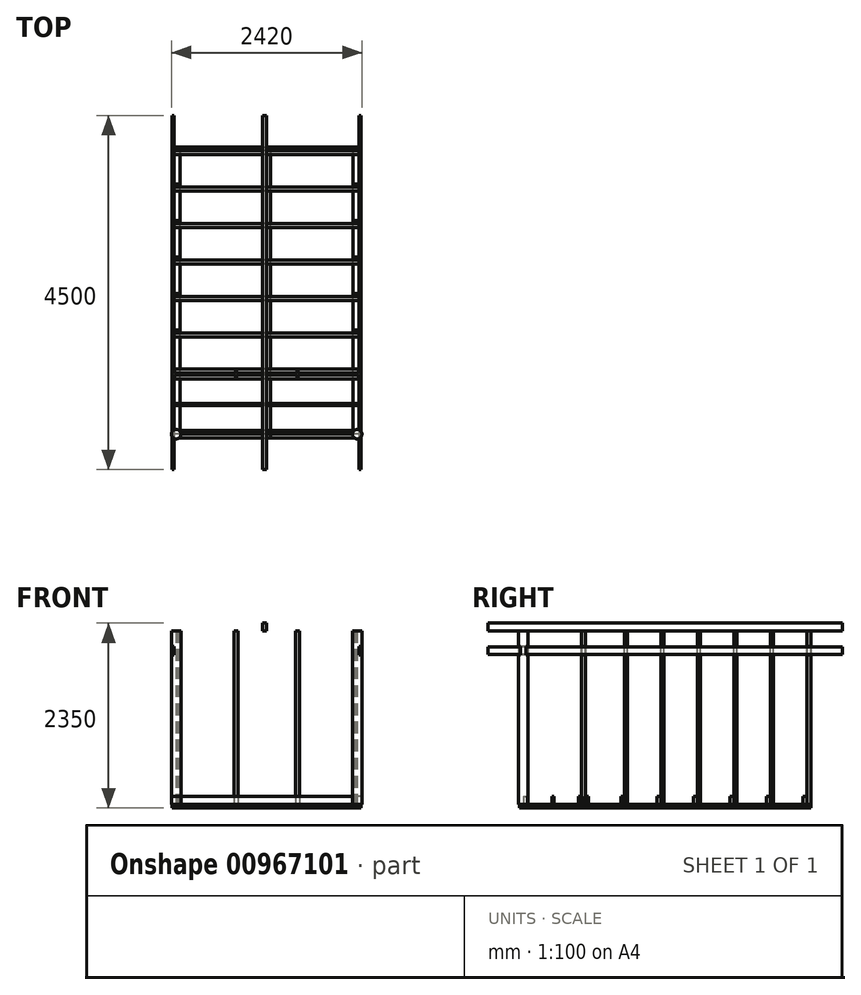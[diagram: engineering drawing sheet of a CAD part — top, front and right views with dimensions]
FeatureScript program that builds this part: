
annotation { "Feature Type Name" : "Feature", "Feature Type Description" : "" }
export const myFeature = defineFeature(function(context is Context, id is Id, definition is map)
    precondition{}
    {
        {
            var Q0;
            Q0=qCreatedBy(makeId("Top.planeOp"),FACE);
            var sketch = newSketch(context, id + "F0", { "sketchPlane" : qUnion([Q0])});
            skLineSegment(sketch, "E0.bottom", {"start": v(-1200, 0) * mm, "end": v(-1100, 0) * mm});
            skLineSegment(sketch, "E0.top", {"start": v(-1200, 3700) * mm, "end": v(-1100, 3700) * mm});
            skLineSegment(sketch, "E0.left", {"start": v(-1200, 0) * mm, "end": v(-1200, 3700) * mm});
            skLineSegment(sketch, "E0.right", {"start": v(-1100, 0) * mm, "end": v(-1100, 3700) * mm});
            skLineSegment(sketch, "E1.bottom", {"start": v(-1099, 0) * mm, "end": v(-51, 0) * mm});
            skLineSegment(sketch, "E1.top", {"start": v(-1099, 100) * mm, "end": v(-51, 100) * mm});
            skLineSegment(sketch, "E1.left", {"start": v(-1099, 0) * mm, "end": v(-1099, 100) * mm});
            skLineSegment(sketch, "E1.right", {"start": v(-51, 0) * mm, "end": v(-51, 100) * mm});
            skLineSegment(sketch, "E2.bottom", {"start": v(-50, 0) * mm, "end": v(50, 0) * mm});
            skLineSegment(sketch, "E2.top", {"start": v(-50, 3700) * mm, "end": v(50, 3700) * mm});
            skLineSegment(sketch, "E2.left", {"start": v(-50, 0) * mm, "end": v(-50, 3700) * mm});
            skLineSegment(sketch, "E2.right", {"start": v(50, 0) * mm, "end": v(50, 3700) * mm});
            skLineSegment(sketch, "E3.bottom", {"start": v(51, 0) * mm, "end": v(1099, 0) * mm});
            skLineSegment(sketch, "E3.top", {"start": v(51, 100) * mm, "end": v(1099, 100) * mm});
            skLineSegment(sketch, "E3.left", {"start": v(51, 0) * mm, "end": v(51, 100) * mm});
            skLineSegment(sketch, "E3.right", {"start": v(1099, 0) * mm, "end": v(1099, 100) * mm});
            skLineSegment(sketch, "E4.bottom", {"start": v(1100, 0) * mm, "end": v(1200, 0) * mm});
            skLineSegment(sketch, "E4.top", {"start": v(1100, 3700) * mm, "end": v(1200, 3700) * mm});
            skLineSegment(sketch, "E4.left", {"start": v(1100, 0) * mm, "end": v(1100, 3700) * mm});
            skLineSegment(sketch, "E4.right", {"start": v(1200, 0) * mm, "end": v(1200, 3700) * mm});
            skLineSegment(sketch, "E5.bottom", {"start": v(51, 3700) * mm, "end": v(1099, 3700) * mm});
            skLineSegment(sketch, "E5.top", {"start": v(51, 3600) * mm, "end": v(1099, 3600) * mm});
            skLineSegment(sketch, "E5.left", {"start": v(51, 3700) * mm, "end": v(51, 3600) * mm});
            skLineSegment(sketch, "E5.right", {"start": v(1099, 3700) * mm, "end": v(1099, 3600) * mm});
            skLineSegment(sketch, "E6.bottom", {"start": v(-1099, 3700) * mm, "end": v(-51, 3700) * mm});
            skLineSegment(sketch, "E6.top", {"start": v(-1099, 3600) * mm, "end": v(-51, 3600) * mm});
            skLineSegment(sketch, "E6.left", {"start": v(-1099, 3700) * mm, "end": v(-1099, 3600) * mm});
            skLineSegment(sketch, "E6.right", {"start": v(-51, 3700) * mm, "end": v(-51, 3600) * mm});
            skLineSegment(sketch, "E7", {"start": v(0, 0) * mm, "end": v(0, 3700) * mm, "construction": true});
            skSolve(sketch);
        }
        {
            var Q0;
            Q0 = qSketchRegion(id + "F0", true);
            extrude(context, id + "F1", {"entities" : qUnion([Q0]), "depth" : 50 * mm, "offsetDistance" : 25 * mm});
        }
        {
            var Q0;
            Q0=qCreatedBy(makeId("Right.planeOp"),FACE);
            var sketch = newSketch(context, id + "F2", { "sketchPlane" : qUnion([Q0])});
            skLineSegment(sketch, "E8.bottom", {"start": v(50, 150) * mm, "end": v(100, 150) * mm});
            skLineSegment(sketch, "E8.top", {"start": v(50, 50) * mm, "end": v(100, 50) * mm});
            skLineSegment(sketch, "E8.left", {"start": v(50, 150) * mm, "end": v(50, 50) * mm});
            skLineSegment(sketch, "E8.right", {"start": v(100, 150) * mm, "end": v(100, 50) * mm});
            skLineSegment(sketch, "E9.bottom", {"start": v(412.5, 150) * mm, "end": v(437.5, 150) * mm});
            skLineSegment(sketch, "E9.top", {"start": v(412.5, 50) * mm, "end": v(437.5, 50) * mm});
            skLineSegment(sketch, "E9.left", {"start": v(412.5, 150) * mm, "end": v(412.5, 50) * mm});
            skLineSegment(sketch, "E9.right", {"start": v(437.5, 150) * mm, "end": v(437.5, 50) * mm});
            skLineSegment(sketch, "E10.bottom", {"start": v(750, 150) * mm, "end": v(800, 150) * mm});
            skLineSegment(sketch, "E10.top", {"start": v(750, 50) * mm, "end": v(800, 50) * mm});
            skLineSegment(sketch, "E10.left", {"start": v(750, 150) * mm, "end": v(750, 50) * mm});
            skLineSegment(sketch, "E10.right", {"start": v(800, 150) * mm, "end": v(800, 50) * mm});
            skLineSegment(sketch, "E11.bottom", {"start": v(825, 150) * mm, "end": v(875, 150) * mm});
            skLineSegment(sketch, "E11.top", {"start": v(825, 50) * mm, "end": v(875, 50) * mm});
            skLineSegment(sketch, "E11.left", {"start": v(825, 150) * mm, "end": v(825, 50) * mm});
            skLineSegment(sketch, "E11.right", {"start": v(875, 150) * mm, "end": v(875, 50) * mm});
            skLineSegment(sketch, "E12.bottom", {"start": v(1287.5, 150) * mm, "end": v(1337.5, 150) * mm});
            skLineSegment(sketch, "E12.top", {"start": v(1287.5, 50) * mm, "end": v(1337.5, 50) * mm});
            skLineSegment(sketch, "E12.left", {"start": v(1287.5, 150) * mm, "end": v(1287.5, 50) * mm});
            skLineSegment(sketch, "E12.right", {"start": v(1337.5, 150) * mm, "end": v(1337.5, 50) * mm});
            skLineSegment(sketch, "E13.bottom", {"start": v(1750, 150) * mm, "end": v(1800, 150) * mm});
            skLineSegment(sketch, "E13.top", {"start": v(1750, 50) * mm, "end": v(1800, 50) * mm});
            skLineSegment(sketch, "E13.left", {"start": v(1750, 150) * mm, "end": v(1750, 50) * mm});
            skLineSegment(sketch, "E13.right", {"start": v(1800, 150) * mm, "end": v(1800, 50) * mm});
            skLineSegment(sketch, "E14.bottom", {"start": v(2212.5, 150) * mm, "end": v(2262.5, 150) * mm});
            skLineSegment(sketch, "E14.top", {"start": v(2212.5, 50) * mm, "end": v(2262.5, 50) * mm});
            skLineSegment(sketch, "E14.left", {"start": v(2212.5, 150) * mm, "end": v(2212.5, 50) * mm});
            skLineSegment(sketch, "E14.right", {"start": v(2262.5, 150) * mm, "end": v(2262.5, 50) * mm});
            skLineSegment(sketch, "E15.bottom", {"start": v(2675, 150) * mm, "end": v(2725, 150) * mm});
            skLineSegment(sketch, "E15.top", {"start": v(2675, 50) * mm, "end": v(2725, 50) * mm});
            skLineSegment(sketch, "E15.left", {"start": v(2675, 150) * mm, "end": v(2675, 50) * mm});
            skLineSegment(sketch, "E15.right", {"start": v(2725, 150) * mm, "end": v(2725, 50) * mm});
            skLineSegment(sketch, "E16.bottom", {"start": v(3137.5, 150) * mm, "end": v(3187.5, 150) * mm});
            skLineSegment(sketch, "E16.top", {"start": v(3137.5, 50) * mm, "end": v(3187.5, 50) * mm});
            skLineSegment(sketch, "E16.left", {"start": v(3137.5, 150) * mm, "end": v(3137.5, 50) * mm});
            skLineSegment(sketch, "E16.right", {"start": v(3187.5, 150) * mm, "end": v(3187.5, 50) * mm});
            skLineSegment(sketch, "E17.bottom", {"start": v(3600, 150) * mm, "end": v(3650, 150) * mm});
            skLineSegment(sketch, "E17.top", {"start": v(3600, 50) * mm, "end": v(3650, 50) * mm});
            skLineSegment(sketch, "E17.left", {"start": v(3600, 150) * mm, "end": v(3600, 50) * mm});
            skLineSegment(sketch, "E17.right", {"start": v(3650, 150) * mm, "end": v(3650, 50) * mm});
            skLineSegment(sketch, "E18", {"start": v(50, 50) * mm, "end": v(100, 150) * mm, "construction": true});
            skLineSegment(sketch, "E19", {"start": v(412.5, 50) * mm, "end": v(437.5, 150) * mm, "construction": true});
            skLineSegment(sketch, "E20", {"start": v(750, 50) * mm, "end": v(800, 150) * mm, "construction": true});
            skLineSegment(sketch, "E21", {"start": v(825, 50) * mm, "end": v(875, 150) * mm, "construction": true});
            skLineSegment(sketch, "E22", {"start": v(1287.5, 50) * mm, "end": v(1337.5, 150) * mm, "construction": true});
            skLineSegment(sketch, "E23", {"start": v(1750, 50) * mm, "end": v(1800, 150) * mm, "construction": true});
            skLineSegment(sketch, "E24", {"start": v(2212.5, 50) * mm, "end": v(2262.5, 150) * mm, "construction": true});
            skLineSegment(sketch, "E25", {"start": v(2675, 50) * mm, "end": v(2725, 150) * mm, "construction": true});
            skLineSegment(sketch, "E26", {"start": v(3137.5, 50) * mm, "end": v(3187.5, 150) * mm, "construction": true});
            skLineSegment(sketch, "E27", {"start": v(3600, 50) * mm, "end": v(3650, 150) * mm, "construction": true});
            skLineSegment(sketch, "E28", {"start": v(3625, 100) * mm, "end": v(3162.5, 100) * mm, "construction": true});
            skLineSegment(sketch, "E29", {"start": v(3162.5, 100) * mm, "end": v(2700, 100) * mm, "construction": true});
            skLineSegment(sketch, "E30", {"start": v(2700, 100) * mm, "end": v(2237.5, 100) * mm, "construction": true});
            skLineSegment(sketch, "E31", {"start": v(2237.5, 100) * mm, "end": v(1775, 100) * mm, "construction": true});
            skLineSegment(sketch, "E32", {"start": v(1775, 100) * mm, "end": v(1312.5, 100) * mm, "construction": true});
            skLineSegment(sketch, "E33", {"start": v(1312.5, 100) * mm, "end": v(850, 100) * mm, "construction": true});
            skLineSegment(sketch, "E34", {"start": v(850, 100) * mm, "end": v(775, 100) * mm, "construction": true});
            skLineSegment(sketch, "E35", {"start": v(775, 100) * mm, "end": v(425, 100) * mm, "construction": true});
            skLineSegment(sketch, "E36", {"start": v(425, 100) * mm, "end": v(75, 100) * mm, "construction": true});
            skSolve(sketch);
        }
        {
            var Q0;
            Q0 = qSketchRegion(id + "F2", true);
            extrude(context, id + "F3", {"entities" : qUnion([Q0]), "endBound" : BoundingType.SYMMETRIC, "depth" : 2400 * mm, "offsetDistance" : 25 * mm});
        }
        {
            var Q0;
            Q0=makeQuery(id+"F1.opExtrude","CAP_FACE",FACE,{"disambiguationData":[OSD([sQuery(id+"F0.wireOp",EDGE,"E2.bottom"),sQuery(id+"F0.wireOp",EDGE,"E2.top"),sQuery(id+"F0.wireOp",EDGE,"E2.left"),sQuery(id+"F0.wireOp",EDGE,"E2.right")])],"isStart":false});
            var sketch = newSketch(context, id + "F4", { "sketchPlane" : qUnion([Q0])});
            skLineSegment(sketch, "E37.bottom", {"start": v(-1200, 3700) * mm, "end": v(-1150, 3700) * mm});
            skLineSegment(sketch, "E37.top", {"start": v(-1200, 3650) * mm, "end": v(-1150, 3650) * mm});
            skLineSegment(sketch, "E37.left", {"start": v(-1200, 3700) * mm, "end": v(-1200, 3650) * mm});
            skLineSegment(sketch, "E37.right", {"start": v(-1150, 3700) * mm, "end": v(-1150, 3650) * mm});
            skLineSegment(sketch, "E38.bottom", {"start": v(1200, 3700) * mm, "end": v(1150, 3700) * mm});
            skLineSegment(sketch, "E38.top", {"start": v(1200, 3650) * mm, "end": v(1150, 3650) * mm});
            skLineSegment(sketch, "E38.left", {"start": v(1200, 3700) * mm, "end": v(1200, 3650) * mm});
            skLineSegment(sketch, "E38.right", {"start": v(1150, 3700) * mm, "end": v(1150, 3650) * mm});
            skLineSegment(sketch, "E39.bottom", {"start": v(1200, 837.5) * mm, "end": v(1150, 837.5) * mm});
            skLineSegment(sketch, "E39.top", {"start": v(1200, 787.5) * mm, "end": v(1150, 787.5) * mm});
            skLineSegment(sketch, "E39.left", {"start": v(1200, 837.5) * mm, "end": v(1200, 787.5) * mm});
            skLineSegment(sketch, "E39.right", {"start": v(1150, 837.5) * mm, "end": v(1150, 787.5) * mm});
            skLineSegment(sketch, "E40", {"start": v(1150, 800) * mm, "end": v(1150, 825) * mm, "construction": true});
            skPoint(sketch, "E41", {"position": v(1150, 812.5) * mm});
            skLineSegment(sketch, "E42.bottom", {"start": v(-1200, 837.5) * mm, "end": v(-1150, 837.5) * mm});
            skLineSegment(sketch, "E42.top", {"start": v(-1200, 787.5) * mm, "end": v(-1150, 787.5) * mm});
            skLineSegment(sketch, "E42.left", {"start": v(-1200, 837.5) * mm, "end": v(-1200, 787.5) * mm});
            skLineSegment(sketch, "E42.right", {"start": v(-1150, 837.5) * mm, "end": v(-1150, 787.5) * mm});
            skLineSegment(sketch, "E43", {"start": v(-1150, 800) * mm, "end": v(-1150, 825) * mm, "construction": true});
            skPoint(sketch, "E44", {"position": v(-1150, 812.5) * mm});
            skLineSegment(sketch, "E45.bottom", {"start": v(-416.67, 3700) * mm, "end": v(-366.67, 3700) * mm});
            skLineSegment(sketch, "E45.top", {"start": v(-416.67, 3650) * mm, "end": v(-366.67, 3650) * mm});
            skLineSegment(sketch, "E45.left", {"start": v(-416.67, 3700) * mm, "end": v(-416.67, 3650) * mm});
            skLineSegment(sketch, "E45.right", {"start": v(-366.67, 3700) * mm, "end": v(-366.67, 3650) * mm});
            skLineSegment(sketch, "E46.bottom", {"start": v(366.67, 3700) * mm, "end": v(416.67, 3700) * mm});
            skLineSegment(sketch, "E46.top", {"start": v(366.67, 3650) * mm, "end": v(416.67, 3650) * mm});
            skLineSegment(sketch, "E46.left", {"start": v(366.67, 3700) * mm, "end": v(366.67, 3650) * mm});
            skLineSegment(sketch, "E46.right", {"start": v(416.67, 3700) * mm, "end": v(416.67, 3650) * mm});
            skLineSegment(sketch, "E47", {"start": v(416.67, 3675) * mm, "end": v(1150, 3675) * mm, "construction": true});
            skLineSegment(sketch, "E48", {"start": v(-366.67, 3675) * mm, "end": v(366.67, 3675) * mm, "construction": true});
            skLineSegment(sketch, "E49", {"start": v(-1150, 3675) * mm, "end": v(-416.67, 3675) * mm, "construction": true});
            skLineSegment(sketch, "E50.bottom", {"start": v(-416.67, 837.5) * mm, "end": v(-366.67, 837.5) * mm});
            skLineSegment(sketch, "E50.top", {"start": v(-416.67, 787.5) * mm, "end": v(-366.67, 787.5) * mm});
            skLineSegment(sketch, "E50.left", {"start": v(-416.67, 837.5) * mm, "end": v(-416.67, 787.5) * mm});
            skLineSegment(sketch, "E50.right", {"start": v(-366.67, 837.5) * mm, "end": v(-366.67, 787.5) * mm});
            skLineSegment(sketch, "E51.bottom", {"start": v(366.67, 837.5) * mm, "end": v(416.67, 837.5) * mm});
            skLineSegment(sketch, "E51.top", {"start": v(366.67, 787.5) * mm, "end": v(416.67, 787.5) * mm});
            skLineSegment(sketch, "E51.left", {"start": v(366.67, 837.5) * mm, "end": v(366.67, 787.5) * mm});
            skLineSegment(sketch, "E51.right", {"start": v(416.67, 837.5) * mm, "end": v(416.67, 787.5) * mm});
            skLineSegment(sketch, "E52", {"start": v(-1150, 812.5) * mm, "end": v(-416.67, 812.5) * mm, "construction": true});
            skLineSegment(sketch, "E53", {"start": v(-366.67, 812.5) * mm, "end": v(366.67, 812.5) * mm, "construction": true});
            skLineSegment(sketch, "E54", {"start": v(416.67, 812.5) * mm, "end": v(1150, 812.5) * mm, "construction": true});
            skCircle(sketch, "E55", {"center": v(-1150, 50) * mm, "radius": 60 * mm});
            skCircle(sketch, "E56", {"center": v(1150, 50) * mm, "radius": 60 * mm});
            skSolve(sketch);
        }
        {
            var Q0;
            Q0 = qSketchRegion(id + "F4", true);
            extrude(context, id + "F5", {"entities" : qUnion([Q0]), "depth" : 2200 * mm, "offsetDistance" : 25 * mm});
        }
        {
            var Q0;
            Q0=makeQuery(id+"F1.opExtrude","CAP_FACE",FACE,{"disambiguationData":[OSD([sQuery(id+"F0.wireOp",EDGE,"E2.bottom"),sQuery(id+"F0.wireOp",EDGE,"E2.top"),sQuery(id+"F0.wireOp",EDGE,"E2.left"),sQuery(id+"F0.wireOp",EDGE,"E2.right")])],"isStart":false});
            var sketch = newSketch(context, id + "F6", { "sketchPlane" : qUnion([Q0])});
            skLineSegment(sketch, "E57.bottom", {"start": v(-1200, 3225) * mm, "end": v(-1125, 3225) * mm});
            skLineSegment(sketch, "E57.top", {"start": v(-1200, 3187.5) * mm, "end": v(-1125, 3187.5) * mm});
            skLineSegment(sketch, "E57.left", {"start": v(-1200, 3225) * mm, "end": v(-1200, 3187.5) * mm});
            skLineSegment(sketch, "E57.right", {"start": v(-1125, 3225) * mm, "end": v(-1125, 3187.5) * mm});
            skLineSegment(sketch, "E58.bottom", {"start": v(-1200, 2762.5) * mm, "end": v(-1125, 2762.5) * mm});
            skLineSegment(sketch, "E58.top", {"start": v(-1200, 2725) * mm, "end": v(-1125, 2725) * mm});
            skLineSegment(sketch, "E58.left", {"start": v(-1200, 2762.5) * mm, "end": v(-1200, 2725) * mm});
            skLineSegment(sketch, "E58.right", {"start": v(-1125, 2762.5) * mm, "end": v(-1125, 2725) * mm});
            skLineSegment(sketch, "E59.bottom", {"start": v(-1200, 2300) * mm, "end": v(-1125, 2300) * mm});
            skLineSegment(sketch, "E59.top", {"start": v(-1200, 2262.5) * mm, "end": v(-1125, 2262.5) * mm});
            skLineSegment(sketch, "E59.left", {"start": v(-1200, 2300) * mm, "end": v(-1200, 2262.5) * mm});
            skLineSegment(sketch, "E59.right", {"start": v(-1125, 2300) * mm, "end": v(-1125, 2262.5) * mm});
            skLineSegment(sketch, "E60.bottom", {"start": v(-1200, 1837.5) * mm, "end": v(-1125, 1837.5) * mm});
            skLineSegment(sketch, "E60.top", {"start": v(-1200, 1800) * mm, "end": v(-1125, 1800) * mm});
            skLineSegment(sketch, "E60.left", {"start": v(-1200, 1837.5) * mm, "end": v(-1200, 1800) * mm});
            skLineSegment(sketch, "E60.right", {"start": v(-1125, 1837.5) * mm, "end": v(-1125, 1800) * mm});
            skLineSegment(sketch, "E61.bottom", {"start": v(-1200, 1375) * mm, "end": v(-1125, 1375) * mm});
            skLineSegment(sketch, "E61.top", {"start": v(-1200, 1337.5) * mm, "end": v(-1125, 1337.5) * mm});
            skLineSegment(sketch, "E61.left", {"start": v(-1200, 1375) * mm, "end": v(-1200, 1337.5) * mm});
            skLineSegment(sketch, "E61.right", {"start": v(-1125, 1375) * mm, "end": v(-1125, 1337.5) * mm});
            skLineSegment(sketch, "E62.bottom", {"start": v(1125, 3225) * mm, "end": v(1200, 3225) * mm});
            skLineSegment(sketch, "E62.top", {"start": v(1125, 3187.5) * mm, "end": v(1200, 3187.5) * mm});
            skLineSegment(sketch, "E62.left", {"start": v(1125, 3225) * mm, "end": v(1125, 3187.5) * mm});
            skLineSegment(sketch, "E62.right", {"start": v(1200, 3225) * mm, "end": v(1200, 3187.5) * mm});
            skLineSegment(sketch, "E63.bottom", {"start": v(1125, 2762.5) * mm, "end": v(1200, 2762.5) * mm});
            skLineSegment(sketch, "E63.top", {"start": v(1125, 2725) * mm, "end": v(1200, 2725) * mm});
            skLineSegment(sketch, "E63.left", {"start": v(1125, 2762.5) * mm, "end": v(1125, 2725) * mm});
            skLineSegment(sketch, "E63.right", {"start": v(1200, 2762.5) * mm, "end": v(1200, 2725) * mm});
            skLineSegment(sketch, "E64.bottom", {"start": v(1125, 2300) * mm, "end": v(1200, 2300) * mm});
            skLineSegment(sketch, "E64.top", {"start": v(1125, 2262.5) * mm, "end": v(1200, 2262.5) * mm});
            skLineSegment(sketch, "E64.left", {"start": v(1125, 2300) * mm, "end": v(1125, 2262.5) * mm});
            skLineSegment(sketch, "E64.right", {"start": v(1200, 2300) * mm, "end": v(1200, 2262.5) * mm});
            skLineSegment(sketch, "E65.bottom", {"start": v(1125, 1837.5) * mm, "end": v(1200, 1837.5) * mm});
            skLineSegment(sketch, "E65.top", {"start": v(1125, 1800) * mm, "end": v(1200, 1800) * mm});
            skLineSegment(sketch, "E65.left", {"start": v(1125, 1837.5) * mm, "end": v(1125, 1800) * mm});
            skLineSegment(sketch, "E65.right", {"start": v(1200, 1837.5) * mm, "end": v(1200, 1800) * mm});
            skLineSegment(sketch, "E66.bottom", {"start": v(1125, 1375) * mm, "end": v(1200, 1375) * mm});
            skLineSegment(sketch, "E66.top", {"start": v(1125, 1337.5) * mm, "end": v(1200, 1337.5) * mm});
            skLineSegment(sketch, "E66.left", {"start": v(1125, 1375) * mm, "end": v(1125, 1337.5) * mm});
            skLineSegment(sketch, "E66.right", {"start": v(1200, 1375) * mm, "end": v(1200, 1337.5) * mm});
            skSolve(sketch);
        }
        {
            var Q0;
            Q0 = qSketchRegion(id + "F6", true);
            extrude(context, id + "F7", {"entities" : qUnion([Q0]), "depth" : 2200 * mm, "offsetDistance" : 25 * mm});
        }
        {
            var Q0;
            Q0=qCreatedBy(makeId("Front.planeOp"),FACE);
            var sketch = newSketch(context, id + "F8", { "sketchPlane" : qUnion([Q0])});
            skLineSegment(sketch, "E67.bottom", {"start": v(-1200, 2051) * mm, "end": v(-1174, 2051) * mm});
            skLineSegment(sketch, "E67.top", {"start": v(-1200, 1949) * mm, "end": v(-1174, 1949) * mm});
            skLineSegment(sketch, "E67.left", {"start": v(-1200, 2051) * mm, "end": v(-1200, 1949) * mm});
            skLineSegment(sketch, "E67.right", {"start": v(-1174, 2051) * mm, "end": v(-1174, 1949) * mm});
            skLineSegment(sketch, "E68.bottom", {"start": v(1174, 2051) * mm, "end": v(1200, 2051) * mm});
            skLineSegment(sketch, "E68.top", {"start": v(1174, 1949) * mm, "end": v(1200, 1949) * mm});
            skLineSegment(sketch, "E68.left", {"start": v(1174, 2051) * mm, "end": v(1174, 1949) * mm});
            skLineSegment(sketch, "E68.right", {"start": v(1200, 2051) * mm, "end": v(1200, 1949) * mm});
            skSolve(sketch);
        }
        {
            var Q0;
            Q0 = qSketchRegion(id + "F8", true);
            extrude(context, id + "F9", {"entities" : qUnion([Q0]), "operationType" : NewBodyOperationType.REMOVE, "endBound" : BoundingType.THROUGH_ALL, "oppositeDirection" : true, "depth" : 25 * mm, "offsetDistance" : 25 * mm, "hasSecondDirection" : true, "secondDirectionBound" : SecondDirectionBoundingType.THROUGH_ALL, "secondDirectionOppositeDirection" : false, "secondDirectionDepth" : 25 * mm});
        }
        {
            var Q0;
            Q0=qCreatedBy(makeId("Front.planeOp"),FACE);
            var sketch = newSketch(context, id + "F10", { "sketchPlane" : qUnion([Q0])});
            skLineSegment(sketch, "E69.bottom", {"start": v(-1200, 2050) * mm, "end": v(-1175, 2050) * mm});
            skLineSegment(sketch, "E69.top", {"start": v(-1200, 1950) * mm, "end": v(-1175, 1950) * mm});
            skLineSegment(sketch, "E69.left", {"start": v(-1200, 2050) * mm, "end": v(-1200, 1950) * mm});
            skLineSegment(sketch, "E69.right", {"start": v(-1175, 2050) * mm, "end": v(-1175, 1950) * mm});
            skLineSegment(sketch, "E70.bottom", {"start": v(1175, 2050) * mm, "end": v(1200, 2050) * mm});
            skLineSegment(sketch, "E70.top", {"start": v(1175, 1950) * mm, "end": v(1200, 1950) * mm});
            skLineSegment(sketch, "E70.left", {"start": v(1175, 2050) * mm, "end": v(1175, 1950) * mm});
            skLineSegment(sketch, "E70.right", {"start": v(1200, 2050) * mm, "end": v(1200, 1950) * mm});
            skLineSegment(sketch, "E71", {"start": v(670.02, 2182.5) * mm, "end": v(1070.02, 2182.5) * mm, "construction": true});
            skLineSegment(sketch, "E72", {"start": v(1070.02, 2182.5) * mm, "end": v(1070.02, 2082.5) * mm, "construction": true});
            skLineSegment(sketch, "E73", {"start": v(0, 2350) * mm, "end": v(1200, 2050) * mm, "construction": true});
            skLineSegment(sketch, "E74.bottom", {"start": v(-50, 2350) * mm, "end": v(0, 2350) * mm});
            skLineSegment(sketch, "E74.top", {"start": v(-50, 2250) * mm, "end": v(0, 2250) * mm});
            skLineSegment(sketch, "E74.left", {"start": v(-50, 2350) * mm, "end": v(-50, 2250) * mm});
            skLineSegment(sketch, "E74.right", {"start": v(0, 2350) * mm, "end": v(0, 2250) * mm});
            skLineSegment(sketch, "E75", {"start": v(-25, 2452.7) * mm, "end": v(-25, 2250) * mm, "construction": true});
            skSolve(sketch);
        }
        {
            var Q0;
            Q0 = qSketchRegion(id + "F10", true);
            extrude(context, id + "F11", {"entities" : qUnion([Q0]), "oppositeDirection" : true, "depth" : 4100 * mm, "offsetDistance" : 25 * mm, "hasSecondDirection" : true, "secondDirectionOppositeDirection" : false, "secondDirectionDepth" : 400 * mm});
        }
    });
